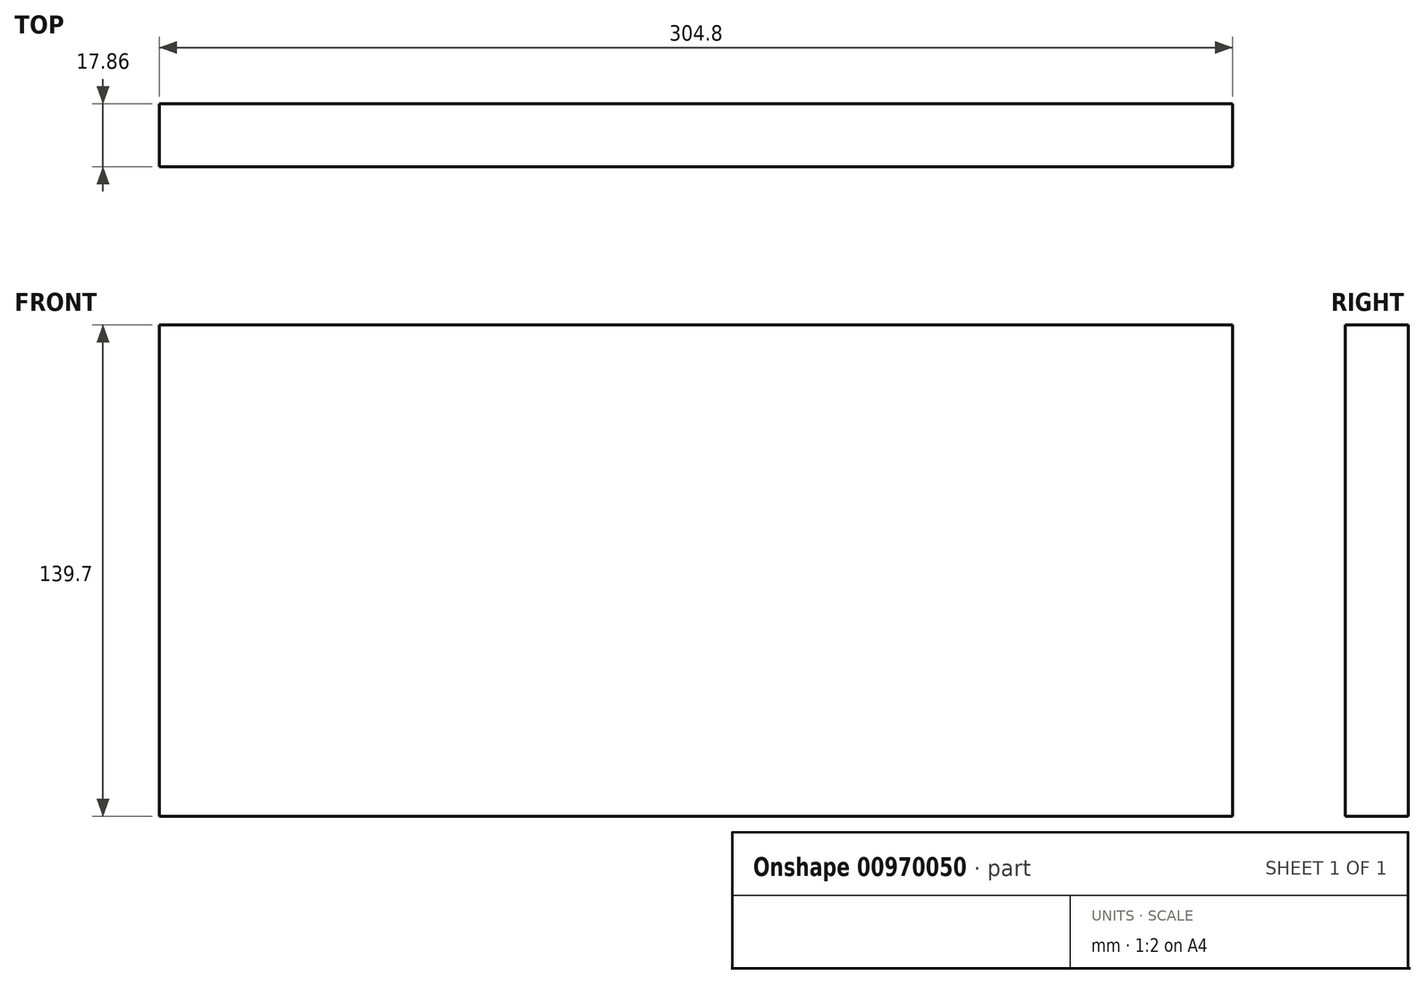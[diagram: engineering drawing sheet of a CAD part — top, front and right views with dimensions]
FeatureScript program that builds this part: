
annotation { "Feature Type Name" : "Feature", "Feature Type Description" : "" }
export const myFeature = defineFeature(function(context is Context, id is Id, definition is map)
    precondition{}
    {
        {
            var Q0;
            Q0=qCreatedBy(makeId("Front.planeOp"),FACE);
            var sketch = newSketch(context, id + "F0", { "sketchPlane" : qUnion([Q0])});
            skLineSegment(sketch, "E0.bottom", {"start": v(152.4, 69.85) * mm, "end": v(-152.4, 69.85) * mm});
            skLineSegment(sketch, "E0.top", {"start": v(152.4, -69.85) * mm, "end": v(-152.4, -69.85) * mm});
            skLineSegment(sketch, "E0.left", {"start": v(152.4, 69.85) * mm, "end": v(152.4, -69.85) * mm});
            skLineSegment(sketch, "E0.right", {"start": v(-152.4, 69.85) * mm, "end": v(-152.4, -69.85) * mm});
            skPoint(sketch, "E0.middle", {"position": v(0, 0) * mm});
            skSolve(sketch);
        }
        {
            var Q0;
            Q0=qSketchRegion(id+"F0",true);
            extrude(context, id + "F1", {"entities" : qUnion([Q0]), "endBound" : BoundingType.SYMMETRIC, "depth" : 17.86 * mm, "offsetDistance" : 25.4 * mm});
        }
    });
